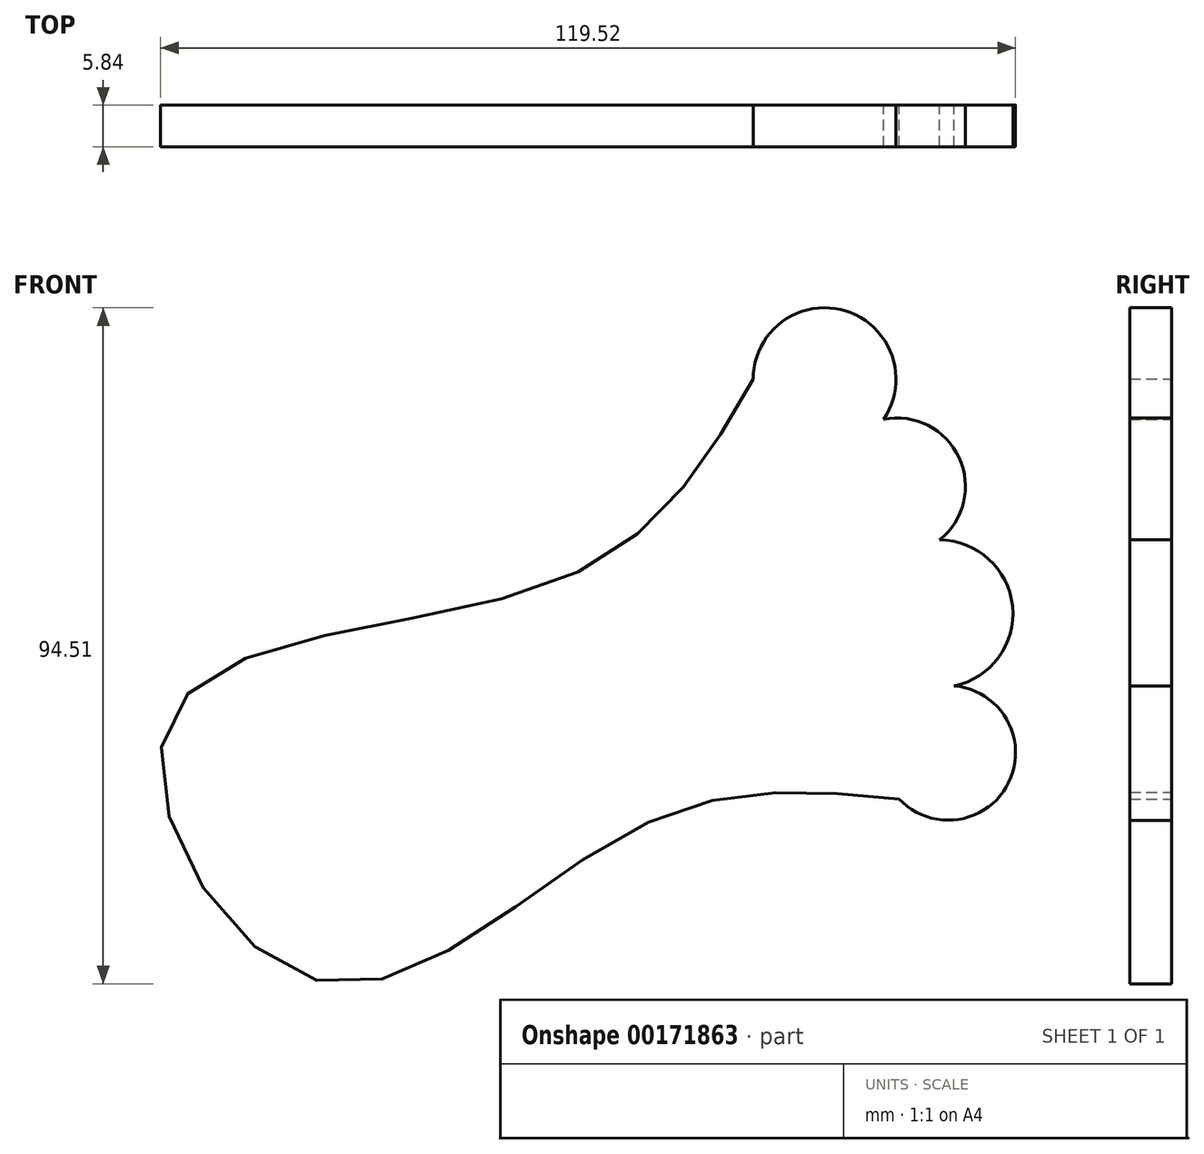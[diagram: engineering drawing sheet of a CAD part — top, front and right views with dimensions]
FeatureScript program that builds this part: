
annotation { "Feature Type Name" : "Feature", "Feature Type Description" : "" }
export const myFeature = defineFeature(function(context is Context, id is Id, definition is map)
    precondition{}
    {
        {
            var Q0;
            Q0=qCreatedBy(makeId("Front.planeOp"),FACE);
            var sketch = newSketch(context, id + "F0", { "sketchPlane" : qUnion([Q0])});
            skArc(sketch, "E0", {"start": v(-47.33, 0) * mm, "mid": v(-32, 2.33) * mm, "end": v(-39.64, 15.82) * mm});
            skArc(sketch, "E1", {"start": v(-39.64, 15.82) * mm, "mid": v(-32.34, 30.16) * mm, "end": v(-47.92, 34.16) * mm});
            skArc(sketch, "E2", {"start": v(-47.92, 34.16) * mm, "mid": v(-39.14, 48.12) * mm, "end": v(-55.6, 48.95) * mm});
            skArc(sketch, "E3", {"start": v(-55.6, 48.95) * mm, "mid": v(-51.5, 66.48) * mm, "end": v(-67.73, 58.71) * mm});
            skFitSpline(sketch, "E4", {"points": [v(-67.73, 58.71) * mm, v(-95.54, 30.32) * mm, v(-149.37, 11.1) * mm, v(-128.96, -25.29) * mm, v(-84, -4) * mm, v(-47.33, 0) * mm], "startDerivative": vector(-102.88, -179.8) * mm, "endDerivative": vector(198.08, -19.93) * mm});
            skSolve(sketch);
        }
        {
            var Q0;
            Q0 = qSketchRegion(id + "F0", true);
            extrude(context, id + "F1", {"entities" : qUnion([Q0]), "depth" : 5.84 * mm});
        }
    });
